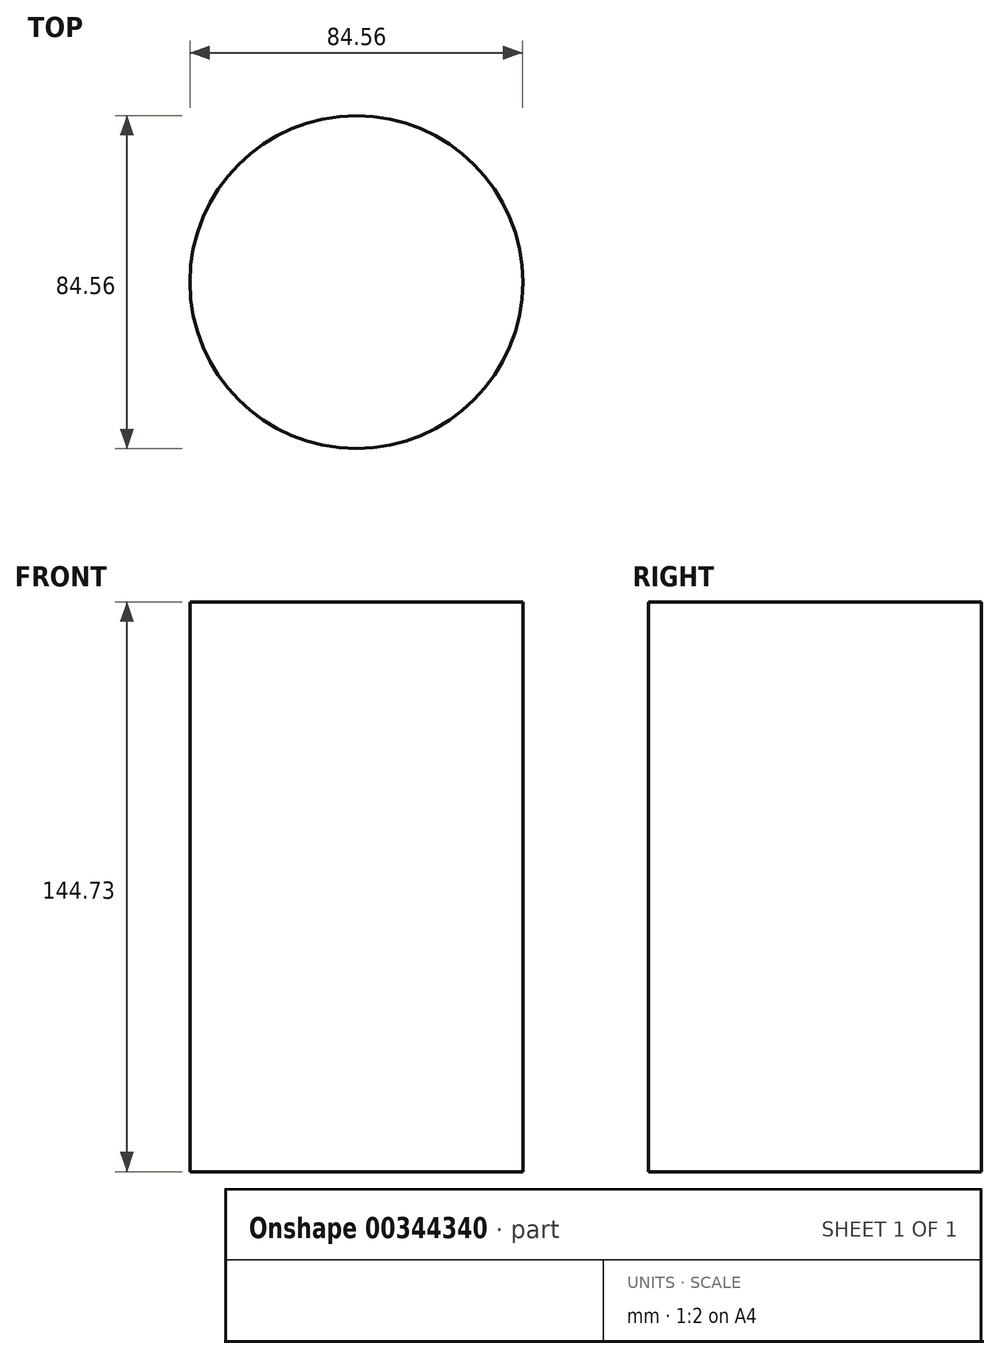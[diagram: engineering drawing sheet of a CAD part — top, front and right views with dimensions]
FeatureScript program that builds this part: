
annotation { "Feature Type Name" : "Feature", "Feature Type Description" : "" }
export const myFeature = defineFeature(function(context is Context, id is Id, definition is map)
    precondition{}
    {
        {
            var Q0;
            Q0=qCreatedBy(makeId("Top.planeOp"),FACE);
            var sketch = newSketch(context, id + "F0", { "sketchPlane" : qUnion([Q0])});
            skCircle(sketch, "E0", {"center": v(0, 0) * mm, "radius": 42.28 * mm});
            skSolve(sketch);
        }
        {
            var Q0;
            Q0=makeQuery(id+"F0.imprint","IMPRINT",FACE,{"disambiguationData":[TD([[makeQuery(id+"F0.imprint","IMPRINT",EDGE,{"derivedFrom":sQuery(id+"F0.wireOp",EDGE,"E0")}),1.0]])]});
            extrude(context, id + "F1", {"entities" : qUnion([Q0]), "depth" : 144.73 * mm});
        }
    });
